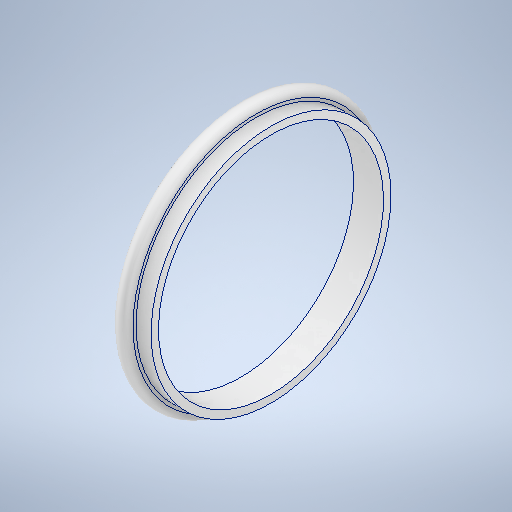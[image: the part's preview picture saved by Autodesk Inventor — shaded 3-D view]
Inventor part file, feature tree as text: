
AUTODESK INVENTOR PART (.ipt)
format: ipt  version: 2025.1 (Build 291241000, 241)  size: 294,912 bytes
history: native  units: mm
features: sketch x2, revolve x1, hole x1
ambient origin geometry x8: Origin, YZ Plane, XZ Plane, XY Plane, X Axis, Y Axis, Z Axis, Center Point
bodies: Solid1 (feature_tree)
feature tree (4):
  revolve  "Revolution1"  [1 undecoded]
  hole  "Hole1"  [1 undecoded]
  sketch  "Sketch1"  dims[d0=5.0mm d5=87.0mm]
  sketch  "Sketch2"  dims[d6=80.0mm d7=5.0mm d8=2.5mm d9=90.0deg d10=75.0mm d11=6.0mm d12=4.0mm d13=2.0mm d14=90.0deg d15=3.5mm d16=0.0mm]
note: 2 required parameter values undecoded (feature->parameter linkage not recoverable at this tier; creation-order binding heuristic only, values carry confidence <= 0.55)